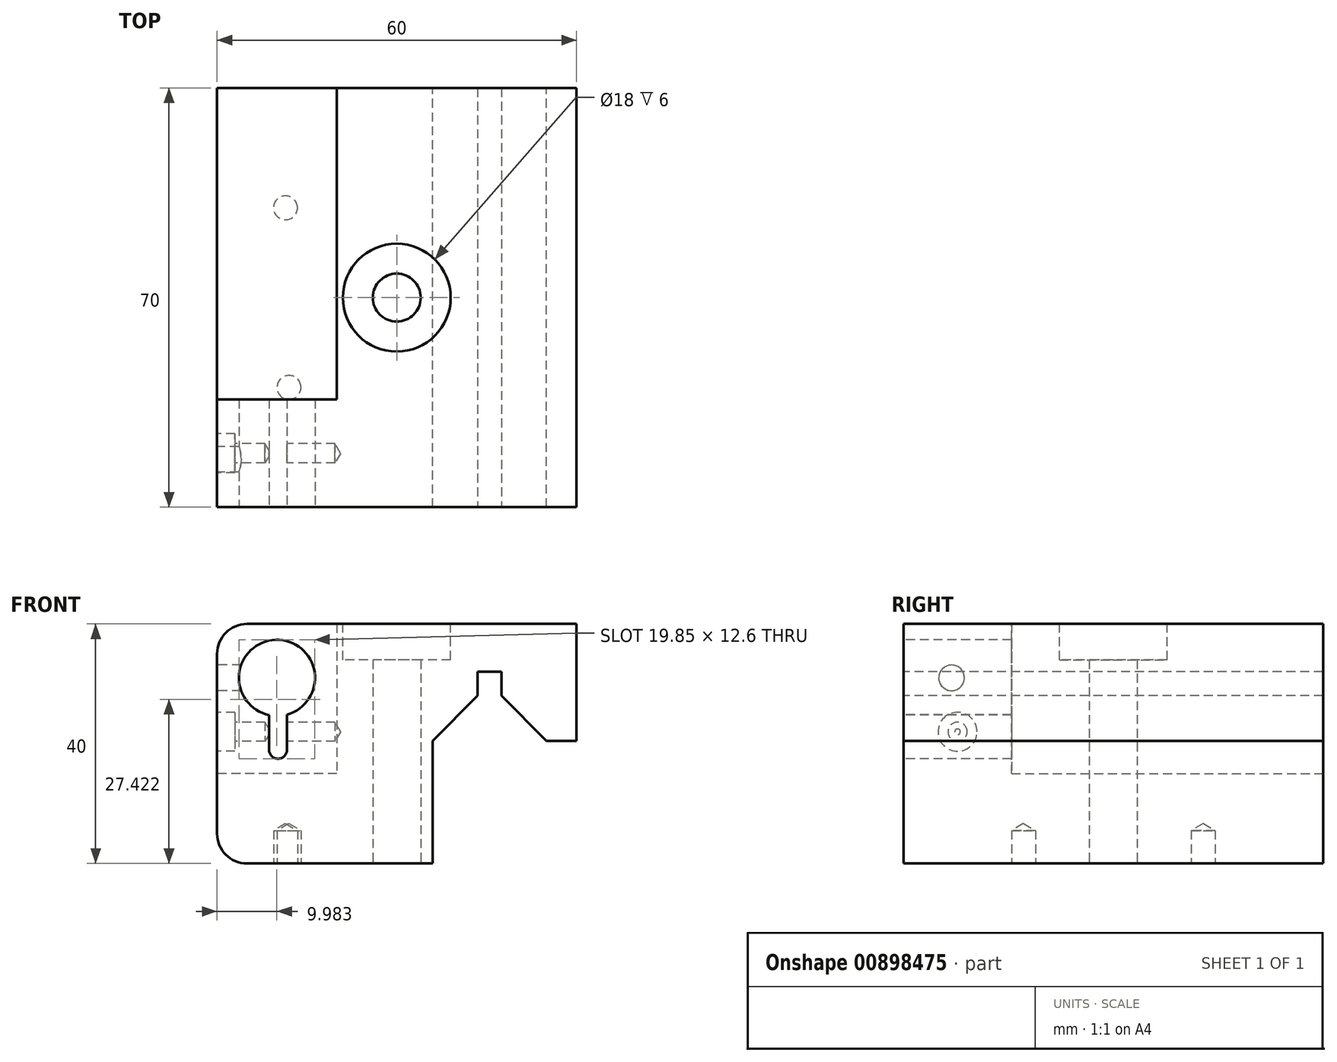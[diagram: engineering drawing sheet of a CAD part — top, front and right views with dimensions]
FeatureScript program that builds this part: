
annotation { "Feature Type Name" : "Feature", "Feature Type Description" : "" }
export const myFeature = defineFeature(function(context is Context, id is Id, definition is map)
    precondition{}
    {
        {
            var Q0;
            Q0=qCreatedBy(makeId("Front.planeOp"),FACE);
            var sketch = newSketch(context, id + "F0", { "sketchPlane" : qUnion([Q0])});
            skLineSegment(sketch, "E0.bottom", {"start": v(-31.74, 22.52) * mm, "end": v(28.26, 22.52) * mm});
            skLineSegment(sketch, "E0.top", {"start": v(-31.74, -17.48) * mm, "end": v(4.26, -17.48) * mm});
            skLineSegment(sketch, "E0.left", {"start": v(-31.74, 22.52) * mm, "end": v(-31.74, -17.48) * mm});
            skLineSegment(sketch, "E0.right", {"start": v(28.26, 22.52) * mm, "end": v(28.26, 3.02) * mm});
            skLineSegment(sketch, "E1", {"start": v(23.26, 3.02) * mm, "end": v(13.76, 12.52) * mm});
            skLineSegment(sketch, "E2", {"start": v(13.76, 12.52) * mm, "end": v(4.26, 3.02) * mm});
            skLineSegment(sketch, "E3", {"start": v(4.26, 3.02) * mm, "end": v(4.26, -9.2) * mm});
            skLineSegment(sketch, "E4", {"start": v(4.26, -9.2) * mm, "end": v(4.26, -17.48) * mm});
            skLineSegment(sketch, "E5", {"start": v(23.26, 3.02) * mm, "end": v(28.26, 3.02) * mm});
            skSolve(sketch);
        }
        {
            var Q0;
            Q0 = qSketchRegion(id + "F0", true);
            extrude(context, id + "F1", {"entities" : qUnion([Q0]), "depth" : 70 * mm, "offsetDistance" : 25 * mm});
        }
        {
            var Q0;
            Q0=makeQuery(id+"F1.opExtrude","CAP_FACE",FACE,{"disambiguationData":[OSD([sQuery(id+"F0.wireOp",EDGE,"E0.bottom"),sQuery(id+"F0.wireOp",EDGE,"E0.top"),sQuery(id+"F0.wireOp",EDGE,"E0.left"),sQuery(id+"F0.wireOp",EDGE,"E0.right"),sQuery(id+"F0.wireOp",EDGE,"E1"),sQuery(id+"F0.wireOp",EDGE,"E2"),sQuery(id+"F0.wireOp",EDGE,"E3"),sQuery(id+"F0.wireOp",EDGE,"E4"),sQuery(id+"F0.wireOp",EDGE,"E5")])],"isStart":true});
            var sketch = newSketch(context, id + "F2", { "sketchPlane" : qUnion([Q0])});
            skLineSegment(sketch, "E6.bottom", {"start": v(11.74, 27.67) * mm, "end": v(39.95, 27.67) * mm});
            skLineSegment(sketch, "E6.top", {"start": v(11.74, -2.48) * mm, "end": v(39.95, -2.48) * mm});
            skLineSegment(sketch, "E6.left", {"start": v(11.74, 27.67) * mm, "end": v(11.74, -2.48) * mm});
            skLineSegment(sketch, "E6.right", {"start": v(39.95, 27.67) * mm, "end": v(39.95, -2.48) * mm});
            skSolve(sketch);
        }
        {
            var Q0;
            Q0 = qSketchRegion(id + "F2", true);
            extrude(context, id + "F3", {"entities" : qUnion([Q0]), "operationType" : NewBodyOperationType.REMOVE, "oppositeDirection" : true, "depth" : 52 * mm, "offsetDistance" : 25 * mm});
        }
        {
            var Q0;
            Q0=makeQuery(id+"F1.opExtrude","SWEPT_EDGE",EDGE,{"disambiguationData":[OSD([sQuery(id+"F0.wireOp",EDGE,"E0.bottom"),sQuery(id+"F0.wireOp",EDGE,"E0.left")])]});
            var Q1;
            Q1=makeQuery(id+"F1.opExtrude","SWEPT_EDGE",EDGE,{"disambiguationData":[OSD([sQuery(id+"F0.wireOp",EDGE,"E0.top"),sQuery(id+"F0.wireOp",EDGE,"E0.left")])]});
            fillet(context, id + "F4", {"entities" : qUnion([Q0, Q1]), "radius" : 5 * mm, "tangentPropagation" : true, "allowEdgeOverflow" : false});
        }
        {
            var Q0;
            Q0=makeQuery(id+"F1.opExtrude","CAP_FACE",FACE,{"disambiguationData":[OSD([sQuery(id+"F0.wireOp",EDGE,"E0.bottom"),sQuery(id+"F0.wireOp",EDGE,"E0.top"),sQuery(id+"F0.wireOp",EDGE,"E0.left"),sQuery(id+"F0.wireOp",EDGE,"E0.right"),sQuery(id+"F0.wireOp",EDGE,"E1"),sQuery(id+"F0.wireOp",EDGE,"E2"),sQuery(id+"F0.wireOp",EDGE,"E3"),sQuery(id+"F0.wireOp",EDGE,"E4"),sQuery(id+"F0.wireOp",EDGE,"E5")])],"isStart":false});
            var sketch = newSketch(context, id + "F5", { "sketchPlane" : qUnion([Q0])});
            skArc(sketch, "E7", {"start": v(-20.06, 7.4) * mm, "mid": v(-21.92, 19.87) * mm, "end": v(-23.06, 7.3) * mm});
            skArc(sketch, "E8.0.endCap", {"start": v(-20.06, 1.52) * mm, "mid": v(-21.56, 0.02) * mm, "end": v(-23.06, 1.52) * mm});
            skLineSegment(sketch, "E8.0.left", {"start": v(-20.06, 7.4) * mm, "end": v(-20.06, 1.52) * mm});
            skLineSegment(sketch, "E8.0.right", {"start": v(-23.06, 7.3) * mm, "end": v(-23.06, 1.52) * mm});
            skPoint(sketch, "E9.orphan", {"position": v(-22.56, 7.52) * mm});
            skSolve(sketch);
        }
        {
            var Q0;
            Q0 = qSketchRegion(id + "F5", true);
            var Q1;
            Q1=makeQuery(id+"F3.boolean.opBoolean","COPY",FACE,{"derivedFrom":makeQuery(id+"F3.opExtrude","CAP_FACE",FACE,{"disambiguationData":[OSD([sQuery(id+"F2.wireOp",EDGE,"E6.bottom"),sQuery(id+"F2.wireOp",EDGE,"E6.top"),sQuery(id+"F2.wireOp",EDGE,"E6.left"),sQuery(id+"F2.wireOp",EDGE,"E6.right")])],"isStart":false})});
            extrude(context, id + "F6", {"entities" : qUnion([Q0]), "operationType" : NewBodyOperationType.REMOVE, "endBound" : BoundingType.UP_TO_SURFACE, "oppositeDirection" : true, "depth" : 25 * mm, "endBoundEntityFace" : qUnion([Q1]), "offsetDistance" : 25 * mm});
        }
        {
            var Q0;
            Q0=makeQuery(id+"F1.opExtrude","CAP_FACE",FACE,{"disambiguationData":[OSD([sQuery(id+"F0.wireOp",EDGE,"E0.bottom"),sQuery(id+"F0.wireOp",EDGE,"E0.top"),sQuery(id+"F0.wireOp",EDGE,"E0.left"),sQuery(id+"F0.wireOp",EDGE,"E0.right"),sQuery(id+"F0.wireOp",EDGE,"E1"),sQuery(id+"F0.wireOp",EDGE,"E2"),sQuery(id+"F0.wireOp",EDGE,"E3"),sQuery(id+"F0.wireOp",EDGE,"E4"),sQuery(id+"F0.wireOp",EDGE,"E5")])],"isStart":false});
            var sketch = newSketch(context, id + "F7", { "sketchPlane" : qUnion([Q0])});
            skLineSegment(sketch, "E10.bottom", {"start": v(11.76, 14.52) * mm, "end": v(15.76, 14.52) * mm});
            skLineSegment(sketch, "E10.top", {"start": v(11.76, 10.52) * mm, "end": v(15.76, 10.52) * mm});
            skLineSegment(sketch, "E10.left", {"start": v(11.76, 14.52) * mm, "end": v(11.76, 10.52) * mm});
            skLineSegment(sketch, "E10.right", {"start": v(15.76, 14.52) * mm, "end": v(15.76, 10.52) * mm});
            skSolve(sketch);
        }
        {
            var Q0;
            Q0 = qSketchRegion(id + "F7", true);
            extrude(context, id + "F8", {"entities" : qUnion([Q0]), "operationType" : NewBodyOperationType.REMOVE, "endBound" : BoundingType.THROUGH_ALL, "oppositeDirection" : true, "depth" : 25 * mm, "offsetDistance" : 25 * mm});
        }
        {
            var Q0;
            Q0=makeQuery(id+"F1.opExtrude","SWEPT_FACE",FACE,{"disambiguationData":[OSD([sQuery(id+"F0.wireOp",EDGE,"E0.top")])]});
            var sketch = newSketch(context, id + "F9", { "sketchPlane" : qUnion([Q0])});
            skCircle(sketch, "E11", {"center": v(-1.74, 35) * mm, "radius": 4 * mm});
            skSolve(sketch);
        }
        {
            var Q0;
            Q0 = qSketchRegion(id + "F9", true);
            extrude(context, id + "F10", {"entities" : qUnion([Q0]), "operationType" : NewBodyOperationType.REMOVE, "endBound" : BoundingType.THROUGH_ALL, "oppositeDirection" : true, "depth" : 25 * mm, "offsetDistance" : 25 * mm});
        }
        {
            var Q0;
            Q0=makeQuery(id+"F1.opExtrude","SWEPT_FACE",FACE,{"disambiguationData":[OSD([sQuery(id+"F0.wireOp",EDGE,"E0.bottom")])]});
            var sketch = newSketch(context, id + "F11", { "sketchPlane" : qUnion([Q0])});
            skCircle(sketch, "E12", {"center": v(-1.74, -35) * mm, "radius": 9 * mm});
            skSolve(sketch);
        }
        {
            var Q0;
            Q0 = qSketchRegion(id + "F11", true);
            extrude(context, id + "F12", {"entities" : qUnion([Q0]), "operationType" : NewBodyOperationType.REMOVE, "oppositeDirection" : true, "depth" : 6 * mm, "offsetDistance" : 25 * mm});
        }
        {
            var Q0;
            Q0=makeQuery(id+"F1.opExtrude","SWEPT_FACE",FACE,{"disambiguationData":[OSD([sQuery(id+"F0.wireOp",EDGE,"E0.top")])]});
            var sketch = newSketch(context, id + "F13", { "sketchPlane" : qUnion([Q0])});
            skPoint(sketch, "E13", {"position": v(-19.72, 50) * mm});
            skPoint(sketch, "E14", {"position": v(-20.3, 20) * mm});
            skSolve(sketch);
        }
        {
            var Q0;
            Q0=sQuery(id+"F13.wireOp",VERTEX,"E13");
            var Q1;
            Q1=sQuery(id+"F13.wireOp",VERTEX,"E14");
            var Q2;
            Q2=makeQuery(id+"F1.opExtrude","SWEPT_BODY",BODY,{"disambiguationData":[OSD([sQuery(id+"F0.wireOp",EDGE,"E0.bottom"),sQuery(id+"F0.wireOp",EDGE,"E0.top"),sQuery(id+"F0.wireOp",EDGE,"E0.left"),sQuery(id+"F0.wireOp",EDGE,"E0.right"),sQuery(id+"F0.wireOp",EDGE,"E1"),sQuery(id+"F0.wireOp",EDGE,"E2"),sQuery(id+"F0.wireOp",EDGE,"E3"),sQuery(id+"F0.wireOp",EDGE,"E4"),sQuery(id+"F0.wireOp",EDGE,"E5")])]});
            hole(context, id + "F14", {"style" : HoleStyle.SIMPLE, "endStyle" : HoleEndStyle.BLIND, "holeDiameter" : 4 * mm, "majorDiameter" : 5 * mm, "holeDepth" : 5.5 * mm, "isTappedThrough" : true, "tappedDepth" : 12 * mm, "tapClearance" : 3, "locations" : qUnion([Q0, Q1]), "scope" : qUnion([Q2])});
        }
        {
            var Q0;
            Q0=makeQuery(id+"F1.opExtrude","SWEPT_FACE",FACE,{"disambiguationData":[OSD([sQuery(id+"F0.wireOp",EDGE,"E0.left")])]});
            var sketch = newSketch(context, id + "F15", { "sketchPlane" : qUnion([Q0])});
            skPoint(sketch, "E15", {"position": v(61, 4.52) * mm});
            skPoint(sketch, "E16", {"position": v(62, 13.52) * mm});
            skSolve(sketch);
        }
        {
            var Q0;
            Q0=makeQuery(id+"F6.boolean.opBoolean","COPY",FACE,{"derivedFrom":makeQuery(id+"F6.opExtrude","SWEPT_FACE",FACE,{"disambiguationData":[OSD([sQuery(id+"F5.wireOp",EDGE,"E8.0.left")])]})});
            var sketch = newSketch(context, id + "F16", { "sketchPlane" : qUnion([Q0])});
            skPoint(sketch, "E17", {"position": v(61, 4.52) * mm});
            skSolve(sketch);
        }
        {
            var Q0;
            Q0=sQuery(id+"F15.wireOp",VERTEX,"E15");
            var Q1;
            Q1=makeQuery(id+"F1.opExtrude","SWEPT_BODY",BODY,{"disambiguationData":[OSD([sQuery(id+"F0.wireOp",EDGE,"E0.bottom"),sQuery(id+"F0.wireOp",EDGE,"E0.top"),sQuery(id+"F0.wireOp",EDGE,"E0.left"),sQuery(id+"F0.wireOp",EDGE,"E0.right"),sQuery(id+"F0.wireOp",EDGE,"E1"),sQuery(id+"F0.wireOp",EDGE,"E2"),sQuery(id+"F0.wireOp",EDGE,"E3"),sQuery(id+"F0.wireOp",EDGE,"E4"),sQuery(id+"F0.wireOp",EDGE,"E5")])]});
            hole(context, id + "F17", {"style" : HoleStyle.C_BORE, "endStyle" : HoleEndStyle.BLIND, "standardTappedOrClearance" : lookupTablePath({ "fit" : "Close", "standard" : "ISO", "size" : "M3", "type" : "Clearance" }), "standardBlindInLast" : lookupTablePath({ "fit" : "Close", "standard" : "ISO", "size" : "M3", "type" : "Clearance" }), "holeDiameter" : 3.2 * mm, "cBoreDiameter" : 6.5 * mm, "cBoreDepth" : 3 * mm, "majorDiameter" : 4 * mm, "holeDepth" : 8 * mm, "isTappedThrough" : true, "tappedDepth" : 12 * mm, "tapClearance" : 3, "locations" : qUnion([Q0]), "scope" : qUnion([Q1])});
        }
        {
            var Q0;
            Q0=sQuery(id+"F16.wireOp",VERTEX,"E17");
            var Q1;
            Q1=makeQuery(id+"F1.opExtrude","SWEPT_BODY",BODY,{"disambiguationData":[OSD([sQuery(id+"F0.wireOp",EDGE,"E0.bottom"),sQuery(id+"F0.wireOp",EDGE,"E0.top"),sQuery(id+"F0.wireOp",EDGE,"E0.left"),sQuery(id+"F0.wireOp",EDGE,"E0.right"),sQuery(id+"F0.wireOp",EDGE,"E1"),sQuery(id+"F0.wireOp",EDGE,"E2"),sQuery(id+"F0.wireOp",EDGE,"E3"),sQuery(id+"F0.wireOp",EDGE,"E4"),sQuery(id+"F0.wireOp",EDGE,"E5")])]});
            hole(context, id + "F18", {"style" : HoleStyle.SIMPLE, "endStyle" : HoleEndStyle.BLIND, "standardTappedOrClearance" : lookupTablePath({ "fit" : "Close", "standard" : "ISO", "size" : "M3", "type" : "Clearance" }), "standardBlindInLast" : lookupTablePath({ "fit" : "Close", "standard" : "ISO", "size" : "M3", "type" : "Clearance" }), "holeDiameter" : 3.2 * mm, "majorDiameter" : 5 * mm, "holeDepth" : 8 * mm, "isTappedThrough" : true, "tappedDepth" : 12 * mm, "tapClearance" : 3, "locations" : qUnion([Q0]), "scope" : qUnion([Q1])});
        }
        {
            var Q0;
            Q0=sQuery(id+"F15.wireOp",VERTEX,"E16");
            var Q1;
            Q1=makeQuery(id+"F1.opExtrude","SWEPT_BODY",BODY,{"disambiguationData":[OSD([sQuery(id+"F0.wireOp",EDGE,"E0.bottom"),sQuery(id+"F0.wireOp",EDGE,"E0.top"),sQuery(id+"F0.wireOp",EDGE,"E0.left"),sQuery(id+"F0.wireOp",EDGE,"E0.right"),sQuery(id+"F0.wireOp",EDGE,"E1"),sQuery(id+"F0.wireOp",EDGE,"E2"),sQuery(id+"F0.wireOp",EDGE,"E3"),sQuery(id+"F0.wireOp",EDGE,"E4"),sQuery(id+"F0.wireOp",EDGE,"E5")])]});
            hole(context, id + "F19", {"style" : HoleStyle.SIMPLE, "endStyle" : HoleEndStyle.BLIND, "standardTappedOrClearance" : lookupTablePath({ "fit" : "Close", "standard" : "ISO", "size" : "M4", "type" : "Clearance" }), "standardBlindInLast" : lookupTablePath({ "fit" : "Close", "standard" : "ISO", "size" : "M4", "type" : "Clearance" }), "holeDiameter" : 4.3 * mm, "majorDiameter" : 5 * mm, "holeDepth" : 8 * mm, "isTappedThrough" : true, "tappedDepth" : 12 * mm, "tapClearance" : 3, "locations" : qUnion([Q0]), "scope" : qUnion([Q1])});
        }
    });
